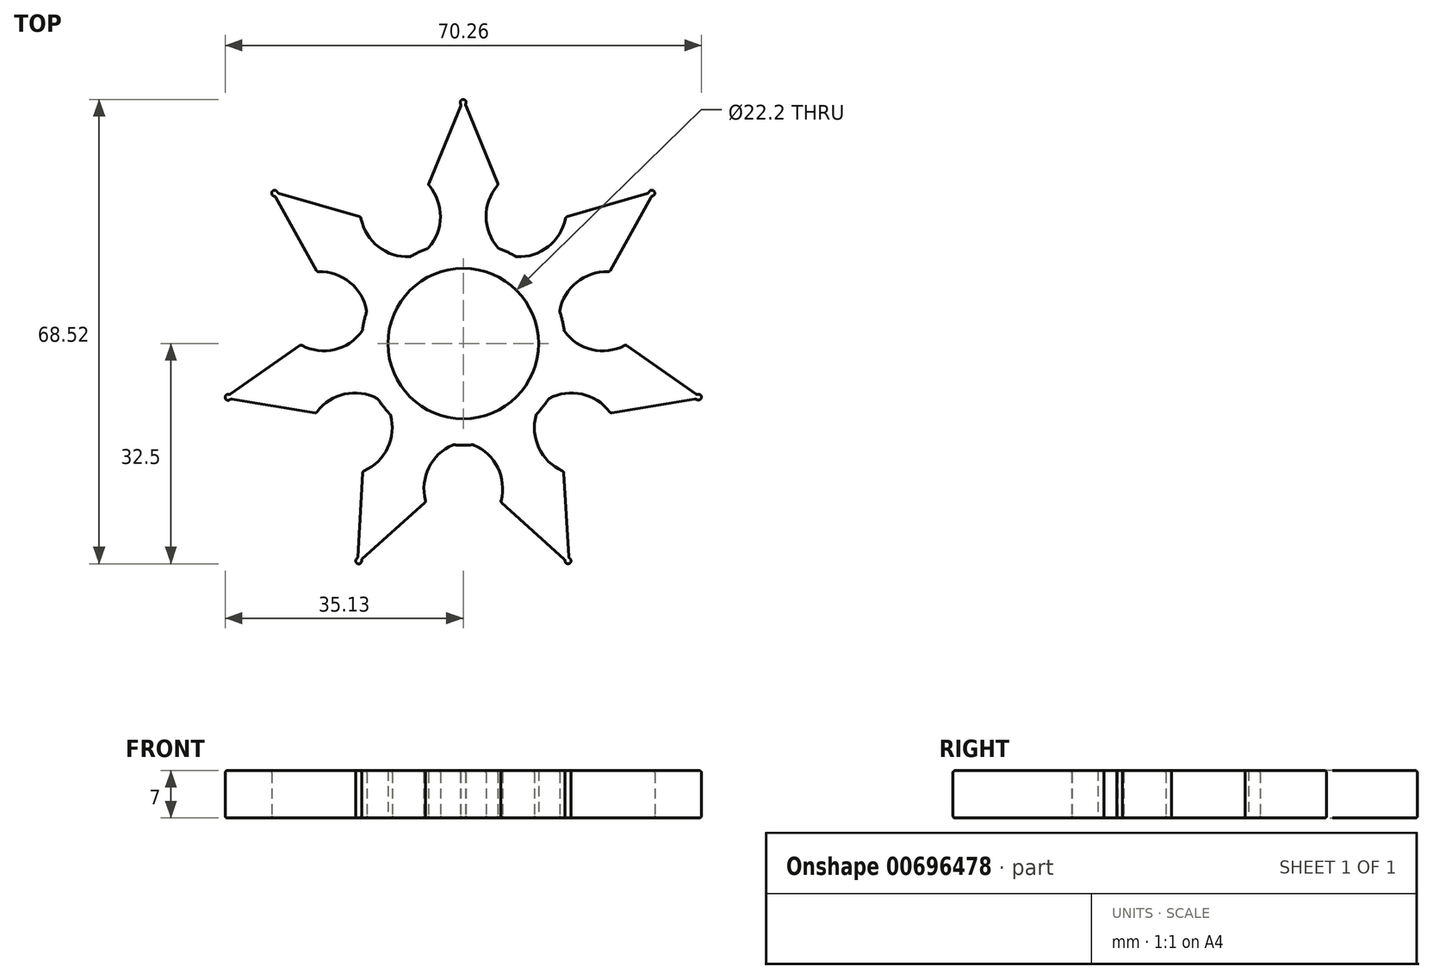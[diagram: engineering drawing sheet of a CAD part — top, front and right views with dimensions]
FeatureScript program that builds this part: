
annotation { "Feature Type Name" : "Feature", "Feature Type Description" : "" }
export const myFeature = defineFeature(function(context is Context, id is Id, definition is map)
    precondition{}
    {
        {
            var Q0;
            Q0=qCreatedBy(makeId("Top.planeOp"),FACE);
            var sketch = newSketch(context, id + "F0", { "sketchPlane" : qUnion([Q0])});
            skCircle(sketch, "E0", {"center": v(0, 0) * mm, "radius": 11.1 * mm});
            skCircle(sketch, "E1", {"center": v(0, 0) * mm, "radius": 15 * mm});
            skPoint(sketch, "E2.end.orphan", {"position": v(5.16, 14.08) * mm});
            skPoint(sketch, "E3.start.orphan", {"position": v(-5.16, 14.08) * mm});
            skPoint(sketch, "E4.start.orphan", {"position": v(0, 15) * mm});
            skPoint(sketch, "E5.end.orphan", {"position": v(5.16, 23.43) * mm});
            skPoint(sketch, "E6.end.orphan", {"position": v(-5.16, 23.43) * mm});
            skArc(sketch, "E7", {"start": v(-5.16, 14.08) * mm, "mid": v(-3.37, 18.76) * mm, "end": v(-5.16, 23.43) * mm});
            skArc(sketch, "E8", {"start": v(5.16, 23.43) * mm, "mid": v(3.37, 18.76) * mm, "end": v(5.16, 14.08) * mm});
            skPoint(sketch, "E9.end.orphan", {"position": v(5.16, 31.08) * mm});
            skLineSegment(sketch, "E10", {"start": v(-0.3, 35.26) * mm, "end": v(-5.16, 23.43) * mm});
            skLineSegment(sketch, "E11", {"start": v(5.16, 23.43) * mm, "end": v(0.3, 35.28) * mm});
            skLineSegment(sketch, "E12.1.0", {"start": v(-15.1, 18.64) * mm, "end": v(-28.15, 22.45) * mm});
            skLineSegment(sketch, "E12.1.1", {"start": v(-28.15, 22.45) * mm, "end": v(-21.54, 10.58) * mm});
            skArc(sketch, "E12.1.2", {"start": v(-15.1, 18.64) * mm, "mid": v(-12.57, 14.33) * mm, "end": v(-7.8, 12.82) * mm});
            skArc(sketch, "E12.1.3", {"start": v(-14.23, 4.75) * mm, "mid": v(-16.77, 9.06) * mm, "end": v(-21.54, 10.58) * mm});
            skLineSegment(sketch, "E12.2.0", {"start": v(-24, -0.18) * mm, "end": v(-35.1, -8.01) * mm});
            skLineSegment(sketch, "E12.2.1", {"start": v(-35.1, -8.01) * mm, "end": v(-21.7, -10.24) * mm});
            skArc(sketch, "E12.2.2", {"start": v(-24, -0.18) * mm, "mid": v(-19.04, -0.89) * mm, "end": v(-14.88, 1.9) * mm});
            skArc(sketch, "E12.2.3", {"start": v(-12.58, -8.16) * mm, "mid": v(-17.54, -7.46) * mm, "end": v(-21.7, -10.24) * mm});
            skLineSegment(sketch, "E12.3.0", {"start": v(-14.82, -18.87) * mm, "end": v(-15.62, -32.43) * mm});
            skLineSegment(sketch, "E12.3.1", {"start": v(-15.62, -32.43) * mm, "end": v(-5.52, -23.35) * mm});
            skArc(sketch, "E12.3.2", {"start": v(-14.82, -18.87) * mm, "mid": v(-11.18, -15.44) * mm, "end": v(-10.76, -10.45) * mm});
            skArc(sketch, "E12.3.3", {"start": v(-1.46, -14.93) * mm, "mid": v(-5.1, -18.36) * mm, "end": v(-5.52, -23.35) * mm});
            skLineSegment(sketch, "E12.4.0", {"start": v(5.52, -23.35) * mm, "end": v(15.62, -32.43) * mm});
            skLineSegment(sketch, "E12.4.1", {"start": v(15.62, -32.43) * mm, "end": v(14.82, -18.87) * mm});
            skArc(sketch, "E12.4.2", {"start": v(5.52, -23.35) * mm, "mid": v(5.1, -18.36) * mm, "end": v(1.46, -14.93) * mm});
            skArc(sketch, "E12.4.3", {"start": v(10.76, -10.45) * mm, "mid": v(11.18, -15.44) * mm, "end": v(14.82, -18.87) * mm});
            skLineSegment(sketch, "E12.5.0", {"start": v(21.7, -10.24) * mm, "end": v(35.1, -8.01) * mm});
            skLineSegment(sketch, "E12.5.1", {"start": v(35.1, -8.01) * mm, "end": v(24, -0.18) * mm});
            skArc(sketch, "E12.5.2", {"start": v(21.7, -10.24) * mm, "mid": v(17.54, -7.46) * mm, "end": v(12.58, -8.16) * mm});
            skArc(sketch, "E12.5.3", {"start": v(14.88, 1.9) * mm, "mid": v(19.04, -0.89) * mm, "end": v(24, -0.18) * mm});
            skLineSegment(sketch, "E12.6.0", {"start": v(21.54, 10.58) * mm, "end": v(28.15, 22.45) * mm});
            skLineSegment(sketch, "E12.6.1", {"start": v(28.15, 22.45) * mm, "end": v(15.1, 18.64) * mm});
            skArc(sketch, "E12.6.2", {"start": v(21.54, 10.58) * mm, "mid": v(16.77, 9.06) * mm, "end": v(14.23, 4.75) * mm});
            skArc(sketch, "E12.6.3", {"start": v(7.8, 12.82) * mm, "mid": v(12.57, 14.33) * mm, "end": v(15.1, 18.64) * mm});
            skPoint(sketch, "E13.start.orphan", {"position": v(0, -1.12) * mm});
            skArc(sketch, "E14", {"start": v(0.3, 35.28) * mm, "mid": v(-0.02, 36.02) * mm, "end": v(-0.3, 35.26) * mm});
            skPoint(sketch, "E15.orphan", {"position": v(0, 36) * mm});
            skArc(sketch, "E16.1.0", {"start": v(-27.4, 22.23) * mm, "mid": v(-28.18, 22.44) * mm, "end": v(-27.76, 21.75) * mm});
            skArc(sketch, "E16.2.0", {"start": v(-34.46, -7.56) * mm, "mid": v(-35.11, -8.04) * mm, "end": v(-34.3, -8.14) * mm});
            skArc(sketch, "E16.3.0", {"start": v(-15.57, -31.65) * mm, "mid": v(-15.6, -32.46) * mm, "end": v(-15.02, -31.9) * mm});
            skArc(sketch, "E16.4.0", {"start": v(15.04, -31.91) * mm, "mid": v(15.65, -32.44) * mm, "end": v(15.57, -31.64) * mm});
            skArc(sketch, "E16.5.0", {"start": v(34.32, -8.14) * mm, "mid": v(35.12, -8) * mm, "end": v(34.44, -7.55) * mm});
            skArc(sketch, "E16.6.0", {"start": v(27.76, 21.76) * mm, "mid": v(28.15, 22.48) * mm, "end": v(27.38, 22.22) * mm});
            skSolve(sketch);
        }
        {
            var Q0;
            Q0 = qSketchRegion(id + "F0", true);
            extrude(context, id + "F1", {"entities" : qUnion([Q0]), "depth" : 7 * mm, "offsetDistance" : 25 * mm});
        }
        {
            var Q0;
            Q0=makeQuery(id+"F1.opExtrude","CAP_EDGE",EDGE,{"disambiguationData":[OSD([sQuery(id+"F0.wireOp",EDGE,"E11")])],"isStart":false});
            var Q1;
            Q1=makeQuery(id+"F1.opExtrude","CAP_EDGE",EDGE,{"disambiguationData":[OSD([sQuery(id+"F0.wireOp",EDGE,"E12.6.2")])],"isStart":false});
            var Q2;
            {var subQ0=sQuery(id+"F0.wireOp",EDGE,"E1");Q2=makeQuery(id+"F1.opExtrude","CAP_EDGE",EDGE,{"disambiguationData":[OSD([subQ0]),TDD([makeQuery(id+"F0.imprint","IMPRINT",EDGE,{"disambiguationData":[TD([[makeQuery(id+"F0.imprint","INTERSECT",VERTEX,{"derivedFrom":[subQ0,sQuery(id+"F0.wireOp",EDGE,"E7")]}),-1.0]])],"derivedFrom":subQ0})])],"isStart":false});}
            var Q3;
            Q3=makeQuery(id+"F1.opExtrude","CAP_EDGE",EDGE,{"disambiguationData":[OSD([sQuery(id+"F0.wireOp",EDGE,"E7")])],"isStart":false});
            var Q4;
            Q4=makeQuery(id+"F1.opExtrude","CAP_EDGE",EDGE,{"disambiguationData":[OSD([sQuery(id+"F0.wireOp",EDGE,"E8")])],"isStart":false});
            var Q5;
            Q5=makeQuery(id+"F1.opExtrude","CAP_EDGE",EDGE,{"disambiguationData":[OSD([sQuery(id+"F0.wireOp",EDGE,"E12.6.1")])],"isStart":false});
            var Q6;
            Q6=makeQuery(id+"F1.opExtrude","CAP_EDGE",EDGE,{"disambiguationData":[OSD([sQuery(id+"F0.wireOp",EDGE,"E12.6.3")])],"isStart":false});
            var Q7;
            {var subQ0=sQuery(id+"F0.wireOp",EDGE,"E1");Q7=makeQuery(id+"F1.opExtrude","CAP_EDGE",EDGE,{"disambiguationData":[OSD([subQ0]),TDD([makeQuery(id+"F0.imprint","IMPRINT",EDGE,{"disambiguationData":[TD([[makeQuery(id+"F0.imprint","INTERSECT",VERTEX,{"derivedFrom":[subQ0,sQuery(id+"F0.wireOp",EDGE,"E8")]}),1.0]])],"derivedFrom":subQ0})])],"isStart":false});}
            var Q8;
            Q8=makeQuery(id+"F1.opExtrude","CAP_EDGE",EDGE,{"disambiguationData":[OSD([sQuery(id+"F0.wireOp",EDGE,"E10")])],"isStart":false});
            var Q9;
            Q9=makeQuery(id+"F1.opExtrude","CAP_EDGE",EDGE,{"disambiguationData":[OSD([sQuery(id+"F0.wireOp",EDGE,"E12.6.1")])],"isStart":true});
            var Q10;
            Q10=makeQuery(id+"F1.opExtrude","SWEPT_EDGE",EDGE,{"disambiguationData":[OSD([sQuery(id+"F0.wireOp",EDGE,"E7"),sQuery(id+"F0.wireOp",EDGE,"E10")])]});
            var Q11;
            Q11=makeQuery(id+"F1.opExtrude","CAP_EDGE",EDGE,{"disambiguationData":[OSD([sQuery(id+"F0.wireOp",EDGE,"E8")])],"isStart":true});
            var Q12;
            Q12=makeQuery(id+"F1.opExtrude","SWEPT_EDGE",EDGE,{"disambiguationData":[OSD([sQuery(id+"F0.wireOp",EDGE,"E12.6.1"),sQuery(id+"F0.wireOp",EDGE,"E12.6.3")])]});
            var Q13;
            Q13=makeQuery(id+"F1.opExtrude","CAP_EDGE",EDGE,{"disambiguationData":[OSD([sQuery(id+"F0.wireOp",EDGE,"E11")])],"isStart":true});
            var Q14;
            Q14=makeQuery(id+"F1.opExtrude","SWEPT_EDGE",EDGE,{"disambiguationData":[OSD([sQuery(id+"F0.wireOp",EDGE,"E1"),sQuery(id+"F0.wireOp",EDGE,"E12.6.3")])]});
            var Q15;
            Q15=makeQuery(id+"F1.opExtrude","SWEPT_EDGE",EDGE,{"disambiguationData":[OSD([sQuery(id+"F0.wireOp",EDGE,"E12.6.0"),sQuery(id+"F0.wireOp",EDGE,"E12.6.2")])]});
            var Q16;
            {var subQ0=sQuery(id+"F0.wireOp",EDGE,"E1");Q16=makeQuery(id+"F1.opExtrude","CAP_EDGE",EDGE,{"disambiguationData":[OSD([subQ0]),TDD([makeQuery(id+"F0.imprint","IMPRINT",EDGE,{"disambiguationData":[TD([[makeQuery(id+"F0.imprint","INTERSECT",VERTEX,{"derivedFrom":[subQ0,sQuery(id+"F0.wireOp",EDGE,"E7")]}),-1.0]])],"derivedFrom":subQ0})])],"isStart":true});}
            var Q17;
            Q17=makeQuery(id+"F1.opExtrude","SWEPT_EDGE",EDGE,{"disambiguationData":[OSD([sQuery(id+"F0.wireOp",EDGE,"E1"),sQuery(id+"F0.wireOp",EDGE,"E12.1.2")])]});
            var Q18;
            Q18=makeQuery(id+"F1.opExtrude","CAP_EDGE",EDGE,{"disambiguationData":[OSD([sQuery(id+"F0.wireOp",EDGE,"E7")])],"isStart":true});
            var Q19;
            Q19=makeQuery(id+"F1.opExtrude","CAP_EDGE",EDGE,{"disambiguationData":[OSD([sQuery(id+"F0.wireOp",EDGE,"E12.6.3")])],"isStart":true});
            var Q20;
            Q20=makeQuery(id+"F1.opExtrude","SWEPT_EDGE",EDGE,{"disambiguationData":[OSD([sQuery(id+"F0.wireOp",EDGE,"E8"),sQuery(id+"F0.wireOp",EDGE,"E11")])]});
            var Q21;
            Q21=makeQuery(id+"F1.opExtrude","SWEPT_EDGE",EDGE,{"disambiguationData":[OSD([sQuery(id+"F0.wireOp",EDGE,"E1"),sQuery(id+"F0.wireOp",EDGE,"E8")])]});
            var Q22;
            Q22=makeQuery(id+"F1.opExtrude","SWEPT_EDGE",EDGE,{"disambiguationData":[OSD([sQuery(id+"F0.wireOp",EDGE,"E1"),sQuery(id+"F0.wireOp",EDGE,"E7")])]});
            var Q23;
            {var subQ0=sQuery(id+"F0.wireOp",EDGE,"E1");Q23=makeQuery(id+"F1.opExtrude","CAP_EDGE",EDGE,{"disambiguationData":[OSD([subQ0]),TDD([makeQuery(id+"F0.imprint","IMPRINT",EDGE,{"disambiguationData":[TD([[makeQuery(id+"F0.imprint","INTERSECT",VERTEX,{"derivedFrom":[subQ0,sQuery(id+"F0.wireOp",EDGE,"E8")]}),1.0]])],"derivedFrom":subQ0})])],"isStart":true});}
            var Q24;
            Q24=makeQuery(id+"F1.opExtrude","CAP_EDGE",EDGE,{"disambiguationData":[OSD([sQuery(id+"F0.wireOp",EDGE,"E10")])],"isStart":true});
            var Q25;
            Q25=makeQuery(id+"F1.opExtrude","CAP_EDGE",EDGE,{"disambiguationData":[OSD([sQuery(id+"F0.wireOp",EDGE,"E12.6.2")])],"isStart":true});
            var Q26;
            Q26=makeQuery(id+"F1.opExtrude","CAP_EDGE",EDGE,{"disambiguationData":[OSD([sQuery(id+"F0.wireOp",EDGE,"E12.1.2")])],"isStart":false});
            var Q27;
            Q27=makeQuery(id+"F1.opExtrude","CAP_EDGE",EDGE,{"disambiguationData":[OSD([sQuery(id+"F0.wireOp",EDGE,"E12.1.3")])],"isStart":false});
            var Q28;
            Q28=makeQuery(id+"F1.opExtrude","CAP_EDGE",EDGE,{"disambiguationData":[OSD([sQuery(id+"F0.wireOp",EDGE,"E12.1.0")])],"isStart":false});
            var Q29;
            {var subQ0=sQuery(id+"F0.wireOp",EDGE,"E1");Q29=makeQuery(id+"F1.opExtrude","CAP_EDGE",EDGE,{"disambiguationData":[OSD([subQ0]),TDD([makeQuery(id+"F0.imprint","IMPRINT",EDGE,{"disambiguationData":[TD([[makeQuery(id+"F0.imprint","INTERSECT",VERTEX,{"derivedFrom":[subQ0,sQuery(id+"F0.wireOp",EDGE,"E12.1.3")]}),-1.0]])],"derivedFrom":subQ0})])],"isStart":false});}
            var Q30;
            Q30=makeQuery(id+"F1.opExtrude","CAP_EDGE",EDGE,{"disambiguationData":[OSD([sQuery(id+"F0.wireOp",EDGE,"E12.2.2")])],"isStart":false});
            var Q31;
            Q31=makeQuery(id+"F1.opExtrude","CAP_EDGE",EDGE,{"disambiguationData":[OSD([sQuery(id+"F0.wireOp",EDGE,"E12.1.1")])],"isStart":false});
            var Q32;
            Q32=makeQuery(id+"F1.opExtrude","SWEPT_EDGE",EDGE,{"disambiguationData":[OSD([sQuery(id+"F0.wireOp",EDGE,"E12.2.0"),sQuery(id+"F0.wireOp",EDGE,"E12.2.2")])]});
            var Q33;
            Q33=makeQuery(id+"F1.opExtrude","CAP_EDGE",EDGE,{"disambiguationData":[OSD([sQuery(id+"F0.wireOp",EDGE,"E12.1.0")])],"isStart":true});
            var Q34;
            Q34=makeQuery(id+"F1.opExtrude","SWEPT_EDGE",EDGE,{"disambiguationData":[OSD([sQuery(id+"F0.wireOp",EDGE,"E12.1.0"),sQuery(id+"F0.wireOp",EDGE,"E12.1.2")])]});
            var Q35;
            {var subQ0=sQuery(id+"F0.wireOp",EDGE,"E1");Q35=makeQuery(id+"F1.opExtrude","CAP_EDGE",EDGE,{"disambiguationData":[OSD([subQ0]),TDD([makeQuery(id+"F0.imprint","IMPRINT",EDGE,{"disambiguationData":[TD([[makeQuery(id+"F0.imprint","INTERSECT",VERTEX,{"derivedFrom":[subQ0,sQuery(id+"F0.wireOp",EDGE,"E12.1.3")]}),-1.0]])],"derivedFrom":subQ0})])],"isStart":true});}
            var Q36;
            Q36=makeQuery(id+"F1.opExtrude","CAP_EDGE",EDGE,{"disambiguationData":[OSD([sQuery(id+"F0.wireOp",EDGE,"E12.2.2")])],"isStart":true});
            var Q37;
            Q37=makeQuery(id+"F1.opExtrude","CAP_EDGE",EDGE,{"disambiguationData":[OSD([sQuery(id+"F0.wireOp",EDGE,"E12.1.1")])],"isStart":true});
            var Q38;
            Q38=makeQuery(id+"F1.opExtrude","CAP_EDGE",EDGE,{"disambiguationData":[OSD([sQuery(id+"F0.wireOp",EDGE,"E12.1.3")])],"isStart":true});
            var Q39;
            Q39=makeQuery(id+"F1.opExtrude","SWEPT_EDGE",EDGE,{"disambiguationData":[OSD([sQuery(id+"F0.wireOp",EDGE,"E1"),sQuery(id+"F0.wireOp",EDGE,"E12.1.3")])]});
            var Q40;
            Q40=makeQuery(id+"F1.opExtrude","CAP_EDGE",EDGE,{"disambiguationData":[OSD([sQuery(id+"F0.wireOp",EDGE,"E12.1.2")])],"isStart":true});
            var Q41;
            Q41=makeQuery(id+"F1.opExtrude","SWEPT_EDGE",EDGE,{"disambiguationData":[OSD([sQuery(id+"F0.wireOp",EDGE,"E1"),sQuery(id+"F0.wireOp",EDGE,"E12.2.2")])]});
            var Q42;
            Q42=makeQuery(id+"F1.opExtrude","SWEPT_EDGE",EDGE,{"disambiguationData":[OSD([sQuery(id+"F0.wireOp",EDGE,"E12.1.1"),sQuery(id+"F0.wireOp",EDGE,"E12.1.3")])]});
            var Q43;
            Q43=makeQuery(id+"F1.opExtrude","CAP_EDGE",EDGE,{"disambiguationData":[OSD([sQuery(id+"F0.wireOp",EDGE,"E12.2.0")])],"isStart":true});
            var Q44;
            Q44=makeQuery(id+"F1.opExtrude","CAP_EDGE",EDGE,{"disambiguationData":[OSD([sQuery(id+"F0.wireOp",EDGE,"E12.2.0")])],"isStart":false});
            var Q45;
            Q45=makeQuery(id+"F1.opExtrude","CAP_EDGE",EDGE,{"disambiguationData":[OSD([sQuery(id+"F0.wireOp",EDGE,"E12.6.0")])],"isStart":false});
            var Q46;
            Q46=makeQuery(id+"F1.opExtrude","CAP_EDGE",EDGE,{"disambiguationData":[OSD([sQuery(id+"F0.wireOp",EDGE,"E12.6.0")])],"isStart":true});
            var Q47;
            Q47=makeQuery(id+"F1.opExtrude","CAP_EDGE",EDGE,{"disambiguationData":[OSD([sQuery(id+"F0.wireOp",EDGE,"E12.5.3")])],"isStart":false});
            var Q48;
            Q48=makeQuery(id+"F1.opExtrude","CAP_EDGE",EDGE,{"disambiguationData":[OSD([sQuery(id+"F0.wireOp",EDGE,"E12.5.2")])],"isStart":false});
            var Q49;
            Q49=makeQuery(id+"F1.opExtrude","CAP_EDGE",EDGE,{"disambiguationData":[OSD([sQuery(id+"F0.wireOp",EDGE,"E12.4.3")])],"isStart":false});
            var Q50;
            {var subQ0=sQuery(id+"F0.wireOp",EDGE,"E1");Q50=makeQuery(id+"F1.opExtrude","CAP_EDGE",EDGE,{"disambiguationData":[OSD([subQ0]),TDD([makeQuery(id+"F0.imprint","IMPRINT",EDGE,{"disambiguationData":[TD([[makeQuery(id+"F0.imprint","INTERSECT",VERTEX,{"derivedFrom":[subQ0,sQuery(id+"F0.wireOp",EDGE,"E12.4.3")]}),-1.0]])],"derivedFrom":subQ0})])],"isStart":false});}
            var Q51;
            {var subQ0=sQuery(id+"F0.wireOp",EDGE,"E1");Q51=makeQuery(id+"F1.opExtrude","CAP_EDGE",EDGE,{"disambiguationData":[OSD([subQ0]),TDD([makeQuery(id+"F0.imprint","IMPRINT",EDGE,{"disambiguationData":[TD([[makeQuery(id+"F0.imprint","INTERSECT",VERTEX,{"derivedFrom":[subQ0,sQuery(id+"F0.wireOp",EDGE,"E12.5.3")]}),-1.0]])],"derivedFrom":subQ0})])],"isStart":false});}
            var Q52;
            Q52=makeQuery(id+"F1.opExtrude","CAP_EDGE",EDGE,{"disambiguationData":[OSD([sQuery(id+"F0.wireOp",EDGE,"E12.5.3")])],"isStart":true});
            var Q53;
            Q53=makeQuery(id+"F1.opExtrude","CAP_EDGE",EDGE,{"disambiguationData":[OSD([sQuery(id+"F0.wireOp",EDGE,"E12.4.3")])],"isStart":true});
            var Q54;
            Q54=makeQuery(id+"F1.opExtrude","SWEPT_EDGE",EDGE,{"disambiguationData":[OSD([sQuery(id+"F0.wireOp",EDGE,"E12.4.1"),sQuery(id+"F0.wireOp",EDGE,"E12.4.3")])]});
            var Q55;
            {var subQ0=sQuery(id+"F0.wireOp",EDGE,"E1");Q55=makeQuery(id+"F1.opExtrude","CAP_EDGE",EDGE,{"disambiguationData":[OSD([subQ0]),TDD([makeQuery(id+"F0.imprint","IMPRINT",EDGE,{"disambiguationData":[TD([[makeQuery(id+"F0.imprint","INTERSECT",VERTEX,{"derivedFrom":[subQ0,sQuery(id+"F0.wireOp",EDGE,"E12.5.3")]}),-1.0]])],"derivedFrom":subQ0})])],"isStart":true});}
            var Q56;
            {var subQ0=sQuery(id+"F0.wireOp",EDGE,"E1");Q56=makeQuery(id+"F1.opExtrude","CAP_EDGE",EDGE,{"disambiguationData":[OSD([subQ0]),TDD([makeQuery(id+"F0.imprint","IMPRINT",EDGE,{"disambiguationData":[TD([[makeQuery(id+"F0.imprint","INTERSECT",VERTEX,{"derivedFrom":[subQ0,sQuery(id+"F0.wireOp",EDGE,"E12.4.3")]}),-1.0]])],"derivedFrom":subQ0})])],"isStart":true});}
            var Q57;
            Q57=makeQuery(id+"F1.opExtrude","SWEPT_EDGE",EDGE,{"disambiguationData":[OSD([sQuery(id+"F0.wireOp",EDGE,"E1"),sQuery(id+"F0.wireOp",EDGE,"E12.5.3")])]});
            var Q58;
            Q58=makeQuery(id+"F1.opExtrude","SWEPT_EDGE",EDGE,{"disambiguationData":[OSD([sQuery(id+"F0.wireOp",EDGE,"E1"),sQuery(id+"F0.wireOp",EDGE,"E12.5.2")])]});
            var Q59;
            Q59=makeQuery(id+"F1.opExtrude","SWEPT_EDGE",EDGE,{"disambiguationData":[OSD([sQuery(id+"F0.wireOp",EDGE,"E12.5.0"),sQuery(id+"F0.wireOp",EDGE,"E12.5.2")])]});
            var Q60;
            Q60=makeQuery(id+"F1.opExtrude","SWEPT_EDGE",EDGE,{"disambiguationData":[OSD([sQuery(id+"F0.wireOp",EDGE,"E12.5.1"),sQuery(id+"F0.wireOp",EDGE,"E12.5.3")])]});
            var Q61;
            Q61=makeQuery(id+"F1.opExtrude","CAP_EDGE",EDGE,{"disambiguationData":[OSD([sQuery(id+"F0.wireOp",EDGE,"E12.5.2")])],"isStart":true});
            var Q62;
            Q62=makeQuery(id+"F1.opExtrude","SWEPT_EDGE",EDGE,{"disambiguationData":[OSD([sQuery(id+"F0.wireOp",EDGE,"E1"),sQuery(id+"F0.wireOp",EDGE,"E12.4.3")])]});
            var Q63;
            Q63=makeQuery(id+"F1.opExtrude","SWEPT_EDGE",EDGE,{"disambiguationData":[OSD([sQuery(id+"F0.wireOp",EDGE,"E1"),sQuery(id+"F0.wireOp",EDGE,"E12.6.2")])]});
            var Q64;
            Q64=makeQuery(id+"F1.opExtrude","CAP_EDGE",EDGE,{"disambiguationData":[OSD([sQuery(id+"F0.wireOp",EDGE,"E12.5.0")])],"isStart":false});
            var Q65;
            Q65=makeQuery(id+"F1.opExtrude","CAP_EDGE",EDGE,{"disambiguationData":[OSD([sQuery(id+"F0.wireOp",EDGE,"E12.5.1")])],"isStart":false});
            var Q66;
            Q66=makeQuery(id+"F1.opExtrude","CAP_EDGE",EDGE,{"disambiguationData":[OSD([sQuery(id+"F0.wireOp",EDGE,"E12.5.1")])],"isStart":true});
            var Q67;
            Q67=makeQuery(id+"F1.opExtrude","CAP_EDGE",EDGE,{"disambiguationData":[OSD([sQuery(id+"F0.wireOp",EDGE,"E12.5.0")])],"isStart":true});
            var Q68;
            {var subQ0=sQuery(id+"F0.wireOp",EDGE,"E1");Q68=makeQuery(id+"F1.opExtrude","CAP_EDGE",EDGE,{"disambiguationData":[OSD([subQ0]),TDD([makeQuery(id+"F0.imprint","IMPRINT",EDGE,{"disambiguationData":[TD([[makeQuery(id+"F0.imprint","INTERSECT",VERTEX,{"derivedFrom":[subQ0,sQuery(id+"F0.wireOp",EDGE,"E12.3.3")]}),-1.0]])],"derivedFrom":subQ0})])],"isStart":false});}
            var Q69;
            Q69=makeQuery(id+"F1.opExtrude","CAP_EDGE",EDGE,{"disambiguationData":[OSD([sQuery(id+"F0.wireOp",EDGE,"E12.3.3")])],"isStart":true});
            var Q70;
            Q70=makeQuery(id+"F1.opExtrude","CAP_EDGE",EDGE,{"disambiguationData":[OSD([sQuery(id+"F0.wireOp",EDGE,"E12.2.3")])],"isStart":false});
            var Q71;
            Q71=makeQuery(id+"F1.opExtrude","CAP_EDGE",EDGE,{"disambiguationData":[OSD([sQuery(id+"F0.wireOp",EDGE,"E12.3.2")])],"isStart":false});
            var Q72;
            Q72=makeQuery(id+"F1.opExtrude","CAP_EDGE",EDGE,{"disambiguationData":[OSD([sQuery(id+"F0.wireOp",EDGE,"E12.3.3")])],"isStart":false});
            var Q73;
            {var subQ0=sQuery(id+"F0.wireOp",EDGE,"E1");Q73=makeQuery(id+"F1.opExtrude","CAP_EDGE",EDGE,{"disambiguationData":[OSD([subQ0]),TDD([makeQuery(id+"F0.imprint","IMPRINT",EDGE,{"disambiguationData":[TD([[makeQuery(id+"F0.imprint","INTERSECT",VERTEX,{"derivedFrom":[subQ0,sQuery(id+"F0.wireOp",EDGE,"E12.3.3")]}),-1.0]])],"derivedFrom":subQ0})])],"isStart":true});}
            var Q74;
            Q74=makeQuery(id+"F1.opExtrude","CAP_EDGE",EDGE,{"disambiguationData":[OSD([sQuery(id+"F0.wireOp",EDGE,"E12.2.3")])],"isStart":true});
            var Q75;
            Q75=makeQuery(id+"F1.opExtrude","CAP_EDGE",EDGE,{"disambiguationData":[OSD([sQuery(id+"F0.wireOp",EDGE,"E12.4.2")])],"isStart":true});
            var Q76;
            Q76=makeQuery(id+"F1.opExtrude","CAP_EDGE",EDGE,{"disambiguationData":[OSD([sQuery(id+"F0.wireOp",EDGE,"E12.4.2")])],"isStart":false});
            var Q77;
            Q77=makeQuery(id+"F1.opExtrude","CAP_EDGE",EDGE,{"disambiguationData":[OSD([sQuery(id+"F0.wireOp",EDGE,"E12.3.2")])],"isStart":true});
            var Q78;
            {var subQ0=sQuery(id+"F0.wireOp",EDGE,"E1");Q78=makeQuery(id+"F1.opExtrude","CAP_EDGE",EDGE,{"disambiguationData":[OSD([subQ0]),TDD([makeQuery(id+"F0.imprint","IMPRINT",EDGE,{"disambiguationData":[TD([[makeQuery(id+"F0.imprint","INTERSECT",VERTEX,{"derivedFrom":[subQ0,sQuery(id+"F0.wireOp",EDGE,"E12.2.3")]}),-1.0]])],"derivedFrom":subQ0})])],"isStart":false});}
            var Q79;
            Q79=makeQuery(id+"F1.opExtrude","SWEPT_EDGE",EDGE,{"disambiguationData":[OSD([sQuery(id+"F0.wireOp",EDGE,"E1"),sQuery(id+"F0.wireOp",EDGE,"E12.2.3")])]});
            var Q80;
            Q80=makeQuery(id+"F1.opExtrude","SWEPT_EDGE",EDGE,{"disambiguationData":[OSD([sQuery(id+"F0.wireOp",EDGE,"E12.3.0"),sQuery(id+"F0.wireOp",EDGE,"E12.3.2")])]});
            var Q81;
            {var subQ0=sQuery(id+"F0.wireOp",EDGE,"E1");Q81=makeQuery(id+"F1.opExtrude","CAP_EDGE",EDGE,{"disambiguationData":[OSD([subQ0]),TDD([makeQuery(id+"F0.imprint","IMPRINT",EDGE,{"disambiguationData":[TD([[makeQuery(id+"F0.imprint","INTERSECT",VERTEX,{"derivedFrom":[subQ0,sQuery(id+"F0.wireOp",EDGE,"E12.2.3")]}),-1.0]])],"derivedFrom":subQ0})])],"isStart":true});}
            var Q82;
            Q82=makeQuery(id+"F1.opExtrude","SWEPT_EDGE",EDGE,{"disambiguationData":[OSD([sQuery(id+"F0.wireOp",EDGE,"E12.3.1"),sQuery(id+"F0.wireOp",EDGE,"E12.3.3")])]});
            var Q83;
            Q83=makeQuery(id+"F1.opExtrude","SWEPT_EDGE",EDGE,{"disambiguationData":[OSD([sQuery(id+"F0.wireOp",EDGE,"E12.4.0"),sQuery(id+"F0.wireOp",EDGE,"E12.4.2")])]});
            var Q84;
            Q84=makeQuery(id+"F1.opExtrude","SWEPT_EDGE",EDGE,{"disambiguationData":[OSD([sQuery(id+"F0.wireOp",EDGE,"E12.2.1"),sQuery(id+"F0.wireOp",EDGE,"E12.2.3")])]});
            var Q85;
            Q85=makeQuery(id+"F1.opExtrude","SWEPT_EDGE",EDGE,{"disambiguationData":[OSD([sQuery(id+"F0.wireOp",EDGE,"E1"),sQuery(id+"F0.wireOp",EDGE,"E12.3.2")])]});
            var Q86;
            Q86=makeQuery(id+"F1.opExtrude","SWEPT_EDGE",EDGE,{"disambiguationData":[OSD([sQuery(id+"F0.wireOp",EDGE,"E1"),sQuery(id+"F0.wireOp",EDGE,"E12.3.3")])]});
            var Q87;
            Q87=makeQuery(id+"F1.opExtrude","SWEPT_EDGE",EDGE,{"disambiguationData":[OSD([sQuery(id+"F0.wireOp",EDGE,"E1"),sQuery(id+"F0.wireOp",EDGE,"E12.4.2")])]});
            var Q88;
            Q88=makeQuery(id+"F1.opExtrude","CAP_EDGE",EDGE,{"disambiguationData":[OSD([sQuery(id+"F0.wireOp",EDGE,"E12.4.1")])],"isStart":false});
            var Q89;
            Q89=makeQuery(id+"F1.opExtrude","CAP_EDGE",EDGE,{"disambiguationData":[OSD([sQuery(id+"F0.wireOp",EDGE,"E12.4.1")])],"isStart":true});
            var Q90;
            Q90=makeQuery(id+"F1.opExtrude","CAP_EDGE",EDGE,{"disambiguationData":[OSD([sQuery(id+"F0.wireOp",EDGE,"E12.4.0")])],"isStart":false});
            var Q91;
            Q91=makeQuery(id+"F1.opExtrude","CAP_EDGE",EDGE,{"disambiguationData":[OSD([sQuery(id+"F0.wireOp",EDGE,"E12.4.0")])],"isStart":true});
            var Q92;
            Q92=makeQuery(id+"F1.opExtrude","CAP_EDGE",EDGE,{"disambiguationData":[OSD([sQuery(id+"F0.wireOp",EDGE,"E12.3.1")])],"isStart":false});
            var Q93;
            Q93=makeQuery(id+"F1.opExtrude","CAP_EDGE",EDGE,{"disambiguationData":[OSD([sQuery(id+"F0.wireOp",EDGE,"E12.3.1")])],"isStart":true});
            var Q94;
            Q94=makeQuery(id+"F1.opExtrude","CAP_EDGE",EDGE,{"disambiguationData":[OSD([sQuery(id+"F0.wireOp",EDGE,"E12.3.0")])],"isStart":false});
            var Q95;
            Q95=makeQuery(id+"F1.opExtrude","CAP_EDGE",EDGE,{"disambiguationData":[OSD([sQuery(id+"F0.wireOp",EDGE,"E12.3.0")])],"isStart":true});
            var Q96;
            Q96=makeQuery(id+"F1.opExtrude","CAP_EDGE",EDGE,{"disambiguationData":[OSD([sQuery(id+"F0.wireOp",EDGE,"E12.2.1")])],"isStart":false});
            var Q97;
            Q97=makeQuery(id+"F1.opExtrude","CAP_EDGE",EDGE,{"disambiguationData":[OSD([sQuery(id+"F0.wireOp",EDGE,"E12.2.1")])],"isStart":true});
            var Q98;
            Q98=makeQuery(id+"F1.opExtrude","SWEPT_FACE",FACE,{"disambiguationData":[OSD([sQuery(id+"F0.wireOp",EDGE,"E16.2.0")])]});
            var Q99;
            Q99=makeQuery(id+"F1.opExtrude","SWEPT_FACE",FACE,{"disambiguationData":[OSD([sQuery(id+"F0.wireOp",EDGE,"E12.2.1")])]});
            var Q100;
            Q100=makeQuery(id+"F1.opExtrude","SWEPT_FACE",FACE,{"disambiguationData":[OSD([sQuery(id+"F0.wireOp",EDGE,"E12.1.0")])]});
            var Q101;
            Q101=makeQuery(id+"F1.opExtrude","SWEPT_EDGE",EDGE,{"disambiguationData":[OSD([sQuery(id+"F0.wireOp",EDGE,"E12.1.1"),sQuery(id+"F0.wireOp",EDGE,"E16.1.0")])]});
            var Q102;
            Q102=makeQuery(id+"F1.opExtrude","SWEPT_EDGE",EDGE,{"disambiguationData":[OSD([sQuery(id+"F0.wireOp",EDGE,"E10"),sQuery(id+"F0.wireOp",EDGE,"E14")])]});
            var Q103;
            Q103=makeQuery(id+"F1.opExtrude","SWEPT_FACE",FACE,{"disambiguationData":[OSD([sQuery(id+"F0.wireOp",EDGE,"E16.1.0")])]});
            var Q104;
            Q104=makeQuery(id+"F1.opExtrude","SWEPT_EDGE",EDGE,{"disambiguationData":[OSD([sQuery(id+"F0.wireOp",EDGE,"E11"),sQuery(id+"F0.wireOp",EDGE,"E14")])]});
            var Q105;
            Q105=makeQuery(id+"F1.opExtrude","SWEPT_FACE",FACE,{"disambiguationData":[OSD([sQuery(id+"F0.wireOp",EDGE,"E16.6.0")])]});
            var Q106;
            Q106=makeQuery(id+"F1.opExtrude","SWEPT_EDGE",EDGE,{"disambiguationData":[OSD([sQuery(id+"F0.wireOp",EDGE,"E12.5.0"),sQuery(id+"F0.wireOp",EDGE,"E16.5.0")])]});
            var Q107;
            Q107=makeQuery(id+"F1.opExtrude","SWEPT_EDGE",EDGE,{"disambiguationData":[OSD([sQuery(id+"F0.wireOp",EDGE,"E12.5.1"),sQuery(id+"F0.wireOp",EDGE,"E16.5.0")])]});
            var Q108;
            Q108=makeQuery(id+"F1.opExtrude","SWEPT_EDGE",EDGE,{"disambiguationData":[OSD([sQuery(id+"F0.wireOp",EDGE,"E12.4.1"),sQuery(id+"F0.wireOp",EDGE,"E16.4.0")])]});
            var Q109;
            Q109=makeQuery(id+"F1.opExtrude","SWEPT_EDGE",EDGE,{"disambiguationData":[OSD([sQuery(id+"F0.wireOp",EDGE,"E12.4.0"),sQuery(id+"F0.wireOp",EDGE,"E16.4.0")])]});
            var Q110;
            Q110=makeQuery(id+"F1.opExtrude","SWEPT_FACE",FACE,{"disambiguationData":[OSD([sQuery(id+"F0.wireOp",EDGE,"E12.3.1")])]});
            var Q111;
            Q111=makeQuery(id+"F1.opExtrude","SWEPT_EDGE",EDGE,{"disambiguationData":[OSD([sQuery(id+"F0.wireOp",EDGE,"E12.3.0"),sQuery(id+"F0.wireOp",EDGE,"E16.3.0")])]});
            var Q112;
            Q112=makeQuery(id+"F1.opExtrude","CAP_EDGE",EDGE,{"disambiguationData":[OSD([sQuery(id+"F0.wireOp",EDGE,"E16.5.0")])],"isStart":false});
            var Q113;
            Q113=makeQuery(id+"F1.opExtrude","CAP_EDGE",EDGE,{"disambiguationData":[OSD([sQuery(id+"F0.wireOp",EDGE,"E16.6.0")])],"isStart":false});
            var Q114;
            Q114=makeQuery(id+"F1.opExtrude","SWEPT_EDGE",EDGE,{"disambiguationData":[OSD([sQuery(id+"F0.wireOp",EDGE,"E12.1.0"),sQuery(id+"F0.wireOp",EDGE,"E16.1.0")])]});
            var Q115;
            Q115=makeQuery(id+"F1.opExtrude","CAP_EDGE",EDGE,{"disambiguationData":[OSD([sQuery(id+"F0.wireOp",EDGE,"E16.2.0")])],"isStart":false});
            var Q116;
            Q116=makeQuery(id+"F1.opExtrude","SWEPT_EDGE",EDGE,{"disambiguationData":[OSD([sQuery(id+"F0.wireOp",EDGE,"E12.2.0"),sQuery(id+"F0.wireOp",EDGE,"E16.2.0")])]});
            var Q117;
            Q117=makeQuery(id+"F1.opExtrude","SWEPT_EDGE",EDGE,{"disambiguationData":[OSD([sQuery(id+"F0.wireOp",EDGE,"E12.2.1"),sQuery(id+"F0.wireOp",EDGE,"E16.2.0")])]});
            var Q118;
            Q118=makeQuery(id+"F1.opExtrude","CAP_EDGE",EDGE,{"disambiguationData":[OSD([sQuery(id+"F0.wireOp",EDGE,"E14")])],"isStart":false});
            var Q119;
            Q119=makeQuery(id+"F1.opExtrude","CAP_EDGE",EDGE,{"disambiguationData":[OSD([sQuery(id+"F0.wireOp",EDGE,"E16.1.0")])],"isStart":false});
            var Q120;
            Q120=makeQuery(id+"F1.opExtrude","CAP_EDGE",EDGE,{"disambiguationData":[OSD([sQuery(id+"F0.wireOp",EDGE,"E16.5.0")])],"isStart":true});
            var Q121;
            Q121=makeQuery(id+"F1.opExtrude","CAP_EDGE",EDGE,{"disambiguationData":[OSD([sQuery(id+"F0.wireOp",EDGE,"E16.6.0")])],"isStart":true});
            var Q122;
            Q122=makeQuery(id+"F1.opExtrude","CAP_EDGE",EDGE,{"disambiguationData":[OSD([sQuery(id+"F0.wireOp",EDGE,"E16.2.0")])],"isStart":true});
            var Q123;
            Q123=makeQuery(id+"F1.opExtrude","SWEPT_EDGE",EDGE,{"disambiguationData":[OSD([sQuery(id+"F0.wireOp",EDGE,"E12.6.0"),sQuery(id+"F0.wireOp",EDGE,"E16.6.0")])]});
            var Q124;
            Q124=makeQuery(id+"F1.opExtrude","CAP_EDGE",EDGE,{"disambiguationData":[OSD([sQuery(id+"F0.wireOp",EDGE,"E14")])],"isStart":true});
            var Q125;
            Q125=makeQuery(id+"F1.opExtrude","SWEPT_EDGE",EDGE,{"disambiguationData":[OSD([sQuery(id+"F0.wireOp",EDGE,"E12.6.1"),sQuery(id+"F0.wireOp",EDGE,"E16.6.0")])]});
            var Q126;
            Q126=makeQuery(id+"F1.opExtrude","CAP_EDGE",EDGE,{"disambiguationData":[OSD([sQuery(id+"F0.wireOp",EDGE,"E16.1.0")])],"isStart":true});
            var Q127;
            Q127=makeQuery(id+"F1.opExtrude","CAP_EDGE",EDGE,{"disambiguationData":[OSD([sQuery(id+"F0.wireOp",EDGE,"E16.3.0")])],"isStart":false});
            var Q128;
            Q128=makeQuery(id+"F1.opExtrude","SWEPT_EDGE",EDGE,{"disambiguationData":[OSD([sQuery(id+"F0.wireOp",EDGE,"E12.3.1"),sQuery(id+"F0.wireOp",EDGE,"E16.3.0")])]});
            var Q129;
            Q129=makeQuery(id+"F1.opExtrude","CAP_EDGE",EDGE,{"disambiguationData":[OSD([sQuery(id+"F0.wireOp",EDGE,"E16.4.0")])],"isStart":false});
            var Q130;
            Q130=makeQuery(id+"F1.opExtrude","CAP_EDGE",EDGE,{"disambiguationData":[OSD([sQuery(id+"F0.wireOp",EDGE,"E16.3.0")])],"isStart":true});
            var Q131;
            Q131=makeQuery(id+"F1.opExtrude","CAP_EDGE",EDGE,{"disambiguationData":[OSD([sQuery(id+"F0.wireOp",EDGE,"E16.4.0")])],"isStart":true});
            fillet(context, id + "F2", {"entities" : qUnion([Q0, Q1, Q2, Q3, Q4, Q5, Q6, Q7, Q8, Q9, Q10, Q11, Q12, Q13, Q14, Q15, Q16, Q17, Q18, Q19, Q20, Q21, Q22, Q23, Q24, Q25, Q26, Q27, Q28, Q29, Q30, Q31, Q32, Q33, Q34, Q35, Q36, Q37, Q38, Q39, Q40, Q41, Q42, Q43, Q44, Q45, Q46, Q47, Q48, Q49, Q50, Q51, Q52, Q53, Q54, Q55, Q56, Q57, Q58, Q59, Q60, Q61, Q62, Q63, Q64, Q65, Q66, Q67, Q68, Q69, Q70, Q71, Q72, Q73, Q74, Q75, Q76, Q77, Q78, Q79, Q80, Q81, Q82, Q83, Q84, Q85, Q86, Q87, Q88, Q89, Q90, Q91, Q92, Q93, Q94, Q95, Q96, Q97, Q98, Q99, Q100, Q101, Q102, Q103, Q104, Q105, Q106, Q107, Q108, Q109, Q110, Q111, Q112, Q113, Q114, Q115, Q116, Q117, Q118, Q119, Q120, Q121, Q122, Q123, Q124, Q125, Q126, Q127, Q128, Q129, Q130, Q131]), "radius" : .34 * mm, "tangentPropagation" : true, "allowEdgeOverflow" : false});
        }
    });
